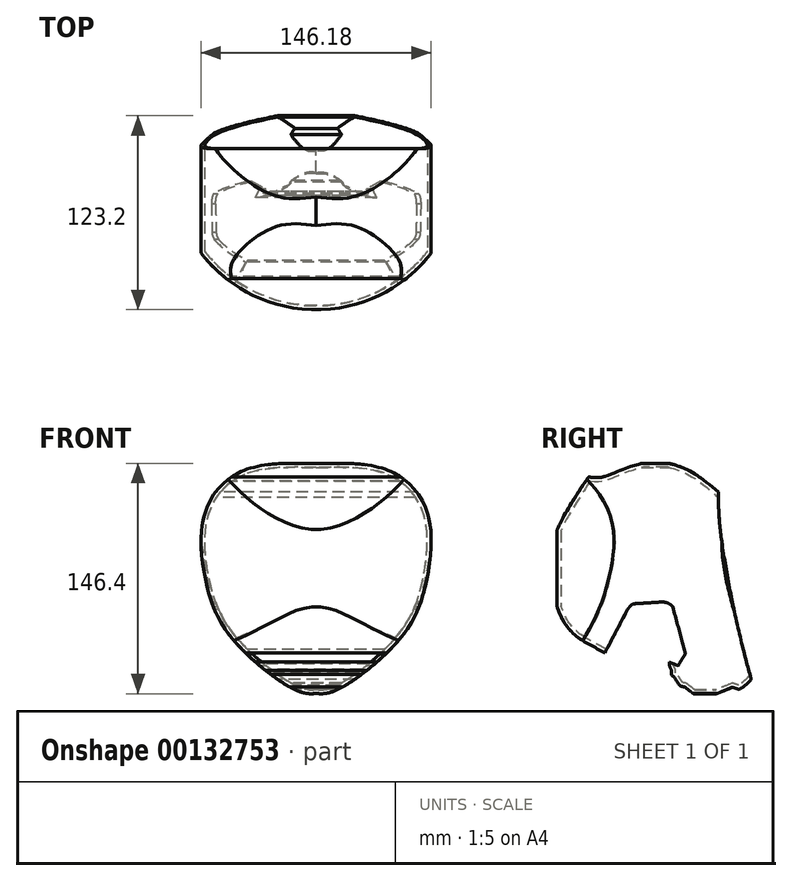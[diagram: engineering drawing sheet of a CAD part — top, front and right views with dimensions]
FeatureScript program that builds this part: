
annotation { "Feature Type Name" : "Feature", "Feature Type Description" : "" }
export const myFeature = defineFeature(function(context is Context, id is Id, definition is map)
    precondition{}
    {
        {
            var Q0;
            Q0=qCreatedBy(makeId("Right.planeOp"),FACE);
            var sketch = newSketch(context, id + "F0", { "sketchPlane" : qUnion([Q0])});
            skLineSegment(sketch, "E0", {"start": v(0, 0) * mm, "end": v(0, 124.62) * mm, "construction": true});
            skLineSegment(sketch, "E1", {"start": v(144.12, 30.02) * mm, "end": v(144.12, -114.74) * mm, "construction": true});
            skFitSpline(sketch, "E2", {"points": [v(-27.76, -26.9) * mm, v(-50.64, -11.55) * mm, v(-61.6, 21.05) * mm, v(-59.42, 47.37) * mm, v(-50.01, 66.49) * mm, v(-38.1, 84.98) * mm], "startDerivative": vector(-109.17, 66.45) * mm, "endDerivative": vector(66.2, 98.28) * mm});
            skFitSpline(sketch, "E3", {"points": [v(-38.1, 84.98) * mm, v(-30.27, 84.66) * mm, v(-17.42, 89.36) * mm, v(3.58, 94.38) * mm, v(25.51, 89.05) * mm, v(44.32, 75.26) * mm], "startDerivative": vector(55.87, -8.63) * mm, "endDerivative": vector(76.9, -65.8) * mm});
            skFitSpline(sketch, "E4", {"points": [v(65.2, -43.62) * mm, v(56.27, -8.44) * mm, v(49.29, 27.02) * mm, v(45.1, 56.06) * mm, v(44.32, 75.26) * mm], "startDerivative": vector(-33.9, 126.72) * mm, "endDerivative": vector(-1.2, 91.24) * mm});
            skFitSpline(sketch, "E5", {"points": [v(65.2, -43.62) * mm, v(61.19, -47.63) * mm, v(57.5, -50.06) * mm], "startDerivative": vector(-7.48, -8.18) * mm, "endDerivative": vector(-7.93, -4.63) * mm});
            skLineSegment(sketch, "E6", {"start": v(57.5, -50.06) * mm, "end": v(53.36, -48.66) * mm});
            skLineSegment(sketch, "E7", {"start": v(53.36, -48.66) * mm, "end": v(37.4, -55.1) * mm});
            skLineSegment(sketch, "E8", {"start": v(37.4, -55.1) * mm, "end": v(34.41, -57.26) * mm});
            skLineSegment(sketch, "E9", {"start": v(34.41, -57.26) * mm, "end": v(22.97, -48.5) * mm});
            skFitSpline(sketch, "E10", {"points": [v(22.97, -48.5) * mm, v(19.92, -47.42) * mm, v(17.34, -43.77) * mm, v(14.6, -40.62) * mm], "startDerivative": vector(-10.86, 1.8) * mm, "endDerivative": vector(-8.38, 8.42) * mm});
            skLineSegment(sketch, "E11", {"start": v(14.6, -40.62) * mm, "end": v(14.6, -37.88) * mm});
            skFitSpline(sketch, "E12", {"points": [v(14.6, -37.88) * mm, v(13.53, -35.64) * mm, v(13.2, -32.65) * mm], "startDerivative": vector(-2.65, 4.47) * mm, "endDerivative": vector(-0.2, 5.97) * mm});
            skLineSegment(sketch, "E13", {"start": v(13.2, -32.65) * mm, "end": v(18.75, -34.97) * mm});
            skLineSegment(sketch, "E14", {"start": v(18.75, -34.97) * mm, "end": v(23.49, -27.33) * mm});
            skLineSegment(sketch, "E15", {"start": v(23.49, -27.33) * mm, "end": v(15.44, 2.4) * mm});
            skFitSpline(sketch, "E16", {"points": [v(15.44, 2.4) * mm, v(12.76, 4.57) * mm, v(9.27, 5.54) * mm], "startDerivative": vector(-5.08, 5) * mm, "endDerivative": vector(-7.26, 1.3) * mm});
            skLineSegment(sketch, "E17", {"start": v(9.27, 5.54) * mm, "end": v(-9, 4.38) * mm});
            skFitSpline(sketch, "E18", {"points": [v(-9, 4.38) * mm, v(-10.76, 3.71) * mm, v(-13.26, 0.81) * mm], "startDerivative": vector(-4.29, -0.95) * mm, "endDerivative": vector(-4.26, -5.9) * mm});
            skLineSegment(sketch, "E19", {"start": v(-13.26, 0.81) * mm, "end": v(-27.76, -26.9) * mm});
            skSolve(sketch);
        }
        {
            var Q0;
            Q0 = qSketchRegion(id + "F0", true);
            extrude(context, id + "F1", {"entities" : qUnion([Q0]), "endBound" : BoundingType.SYMMETRIC, "depth" : 189.84 * mm});
        }
        {
            var Q0;
            Q0=qCreatedBy(makeId("Front.planeOp"),FACE);
            var sketch = newSketch(context, id + "F2", { "sketchPlane" : qUnion([Q0])});
            skFitSpline(sketch, "E20", {"points": [v(0, 93.39) * mm, v(46.87, 88.64) * mm, v(70.6, 62.29) * mm, v(70.06, 18.54) * mm, v(53.2, -17.82) * mm, v(11.56, -51.03) * mm, v(0, -52.61) * mm], "startDerivative": vector(269.04, 7.1) * mm, "endDerivative": vector(-103.7, 7.84) * mm});
            skFitSpline(sketch, "E21.MirrorCS", {"points": [v(0, 93.39) * mm, v(-46.87, 88.64) * mm, v(-70.6, 62.29) * mm, v(-70.06, 18.54) * mm, v(-53.2, -17.82) * mm, v(-11.56, -51.03) * mm, v(0, -52.61) * mm], "startDerivative": vector(-269.04, 7.1) * mm, "endDerivative": vector(103.7, 7.84) * mm});
            skSolve(sketch);
        }
        {
            var Q0;
            Q0 = qSketchRegion(id + "F2", true);
            extrude(context, id + "F3", {"entities" : qUnion([Q0]), "operationType" : NewBodyOperationType.INTERSECT, "endBound" : BoundingType.SYMMETRIC, "depth" : 302.72 * mm});
        }
        {
            var Q0;
            Q0=qCreatedBy(makeId("Top.planeOp"),FACE);
            var sketch = newSketch(context, id + "F4", { "sketchPlane" : qUnion([Q0])});
            skLineSegment(sketch, "E22", {"start": v(73.09, 46.54) * mm, "end": v(73.09, -60.34) * mm, "construction": true});
            skLineSegment(sketch, "E23", {"start": v(-73.09, -60.34) * mm, "end": v(-73.09, 46.54) * mm, "construction": true});
            skLineSegment(sketch, "E24.0", {"start": v(24.5, 65.2) * mm, "end": v(-24.5, 65.2) * mm});
            skLineSegment(sketch, "E25", {"start": v(73.09, 46.54) * mm, "end": v(73.09, -21.95) * mm});
            skLineSegment(sketch, "E26", {"start": v(-73.09, 46.54) * mm, "end": v(-73.09, -21.95) * mm});
            skPoint(sketch, "E27.0.end.orphan", {"position": v(63.95, 44.32) * mm});
            skPoint(sketch, "E28.0.end.orphan", {"position": v(-63.95, 44.32) * mm});
            skArc(sketch, "E29", {"start": v(-73.09, -21.95) * mm, "mid": v(0, -58) * mm, "end": v(73.09, -21.95) * mm});
            skFitSpline(sketch, "E30", {"points": [v(73.09, 46.54) * mm, v(58.98, 57.44) * mm, v(34.03, 63.5) * mm, v(24.5, 65.2) * mm], "startDerivative": vector(-34.79, 35.67) * mm, "endDerivative": vector(-32.08, 6.14) * mm});
            skFitSpline(sketch, "E31.MirrorCS", {"points": [v(-73.09, 46.54) * mm, v(-58.98, 57.44) * mm, v(-34.03, 63.5) * mm, v(-24.5, 65.2) * mm], "startDerivative": vector(34.79, 35.67) * mm, "endDerivative": vector(32.08, 6.14) * mm});
            skSolve(sketch);
        }
        {
            var Q0;
            Q0 = qSketchRegion(id + "F4", true);
            extrude(context, id + "F5", {"entities" : qUnion([Q0]), "operationType" : NewBodyOperationType.INTERSECT, "endBound" : BoundingType.SYMMETRIC, "depth" : 236.7 * mm});
        }
        {
            var Q0;
            Q0=makeQuery(id+"F1.opExtrude","SWEPT_FACE",FACE,{"disambiguationData":[OSD([sQuery(id+"F0.wireOp",EDGE,"E4")])]});
            var Q1;
            Q1=makeQuery(id+"F1.opExtrude","SWEPT_FACE",FACE,{"disambiguationData":[OSD([sQuery(id+"F0.wireOp",EDGE,"E19")])]});
            var Q2;
            Q2=makeQuery(id+"F1.opExtrude","SWEPT_FACE",FACE,{"disambiguationData":[OSD([sQuery(id+"F0.wireOp",EDGE,"E18")])]});
            var Q3;
            Q3=makeQuery(id+"F1.opExtrude","SWEPT_FACE",FACE,{"disambiguationData":[OSD([sQuery(id+"F0.wireOp",EDGE,"E17")])]});
            var Q4;
            Q4=makeQuery(id+"F1.opExtrude","SWEPT_FACE",FACE,{"disambiguationData":[OSD([sQuery(id+"F0.wireOp",EDGE,"E16")])]});
            var Q5;
            Q5=makeQuery(id+"F1.opExtrude","SWEPT_FACE",FACE,{"disambiguationData":[OSD([sQuery(id+"F0.wireOp",EDGE,"E15")])]});
            var Q6;
            Q6=makeQuery(id+"F1.opExtrude","SWEPT_FACE",FACE,{"disambiguationData":[OSD([sQuery(id+"F0.wireOp",EDGE,"E14")])]});
            var Q7;
            Q7=makeQuery(id+"F1.opExtrude","SWEPT_FACE",FACE,{"disambiguationData":[OSD([sQuery(id+"F0.wireOp",EDGE,"E13")])]});
            shell(context, id + "F6", {"entities" : qUnion([Q0, Q1, Q2, Q3, Q4, Q5, Q6, Q7]), "thickness" : 2.5 * mm});
        }
    });
